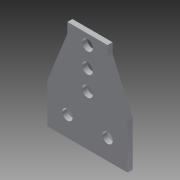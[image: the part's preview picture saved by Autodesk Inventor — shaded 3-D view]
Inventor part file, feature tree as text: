
AUTODESK INVENTOR PART (.ipt)
format: ipt  version: 2013 (Build 170138000, 138)  size: 104,448 bytes
history: native  units: in
note: dims shown in document units (in); Inventor stores cm internally (conversion verified against a paired STEP export)
features: reference x5, extrude x3, sketch x3
ambient origin geometry x8: Origin, YZ Plane, XZ Plane, XY Plane, X Axis, Y Axis, Z Axis, Center Point
bodies: Solid1 (feature_tree)
feature tree (11):
  extrude  "Extrusion1"  Depth=2.25in
  extrude  "Extrusion2"  Depth=0.5in
  extrude  "Extrusion3"  Depth=0.125in TaperAngle=0.0deg
  sketch  "Sketch1"  dims[d0=2.0in d1=2.25in]
  sketch  "Sketch2"  dims[d2=1.0in d3=0.5in]
  sketch  "Sketch3"  dims[d4=0.5in d5=0.125in d6=0.0in d7=0.25in d8=0.125in d9=0.0in d10=0.125in d11=0.0in]
  reference  "Reference1"
  reference  "Reference2"
  reference  "Reference3"
  reference  "Reference4"
  reference  "Reference5"
